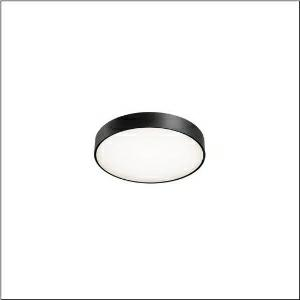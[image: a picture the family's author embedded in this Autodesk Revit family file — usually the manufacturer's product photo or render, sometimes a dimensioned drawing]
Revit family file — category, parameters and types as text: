
# Revit family: round_21_s_51mr34fd0321b
name_source: partatom
category: Lighting Fixtures
units: mm (PartAtom-declared; Revit-internal decimal feet)

## family parameters
Cut with Voids When Loaded = No
Host = Face
Light Source = No
Part Type = Normal
Room Calculation Point = No
Round Connector Dimension = Use Diameter
Shared = No

## types (1)
- Round 21 S (1 x LED, 3750 lm, 30.3 W, 3000K)
    Apparent Load = 30 VA
    CIE Flux Codes = 49 80 96 100 100
    Color Rendering = 80
    Color Temperature = 3000K
    Default Elevation = 1800 mm
    Description = Round 21 S, wall and ceiling luminaire, primary optical cover: cover, of PMMA, opal, light emission: direct distribution, primary light characteristic: symmetric, installation type: suspended mounting, surface-mounted, LED, rated luminous flux: 3.750lm, luminous efficacy: 124lm/W, light colour: 830, colour temperature: 3000K, control gear: DALI 2, with terminal, 5-pole, mains connection: 230V, AC, 50/60Hz, rated input power: 30.3W, housing, of aluminium, coated, black, diameter: 400mm, height: 62mm, protection rating (complete): IP40, insulation class (complete): insulation class I (protective earthing), certification: CE, impact resistance: IK04, permissible operating ambient temperature: -10..+35°C, packaging unit: 1 piece
    Height = 87 mm
    Lamp = 1 x LED
    Lamp Light Flux = 3750 lm
    Lamp Power = 30.3 W
    Lamp count = 1
    Length = 400 mm
    Luminous efficacy = 124 lm/W
    Manufacturer = Siteco
    ModVariant = No
    Model = 51MR34FD0321B
    Mounting Place = Ceiling
    Mounting Type = Surface mounted
    Number of Poles = 1
    OnlyDefault = Yes
    Power Factor = 1
    Product Name = Round 21 S
    Product group = wall and ceiling luminaire
    ProductGroupID = 304
    Protection Class = Protection class I
    Protection Degree = IP 40
    RLX_Detail_Level = 1
    RLX_Emergency_Light_Flux = 0 lm
    RLX_Emergency_Type = 0
    RLX_Emergency_Type_DB = No
    RlxData = <blob elided: 13453 chars, md5=d9cf7cfe>
    Socket = socket
    Standby Power = 0 W
    System Light Flux = 3750 lm
    System Power = 30 W
    Type Comments = Product without accessories
    Type Image = l_1258311.jpg
    URL = http://relux.com
    VarID = ---
    Voltage = 0 V
    Weight = 0.00 kg
    Width = 0 mm  [stored 0 ft]

note: [stored X ft] marks values corroborated as IEEE doubles in the binary element streams (Revit-internal decimal feet)

## geometry (parser evidence)
native form markers: Sweep x11
no freeform markers — native parametric forms only
